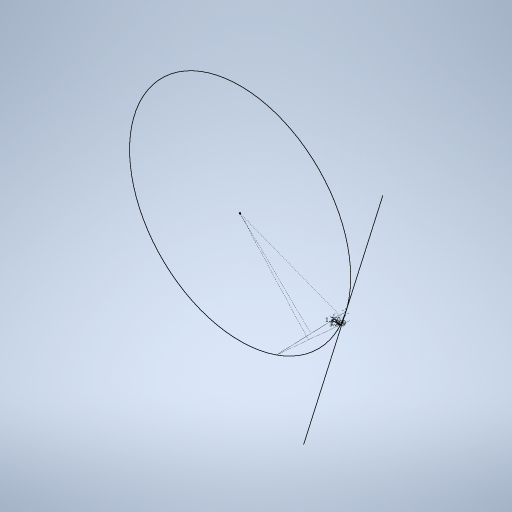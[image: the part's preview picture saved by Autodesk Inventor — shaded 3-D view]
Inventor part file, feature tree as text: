
AUTODESK INVENTOR PART (.ipt)
format: ipt  version: 2024 (Build 280153000, 153)  size: 246,272 bytes
history: native  units: in
note: dims shown in document units (in); Inventor stores cm internally (conversion verified against a paired STEP export)
features: sketch x1
ambient origin geometry x8: Origin, YZ Plane, XZ Plane, XY Plane, X Axis, Y Axis, Z Axis, Center Point
feature tree (1):
  sketch  "Sketch1"  dims[d0=1.25in d2=2.5in d3=3.2in]
